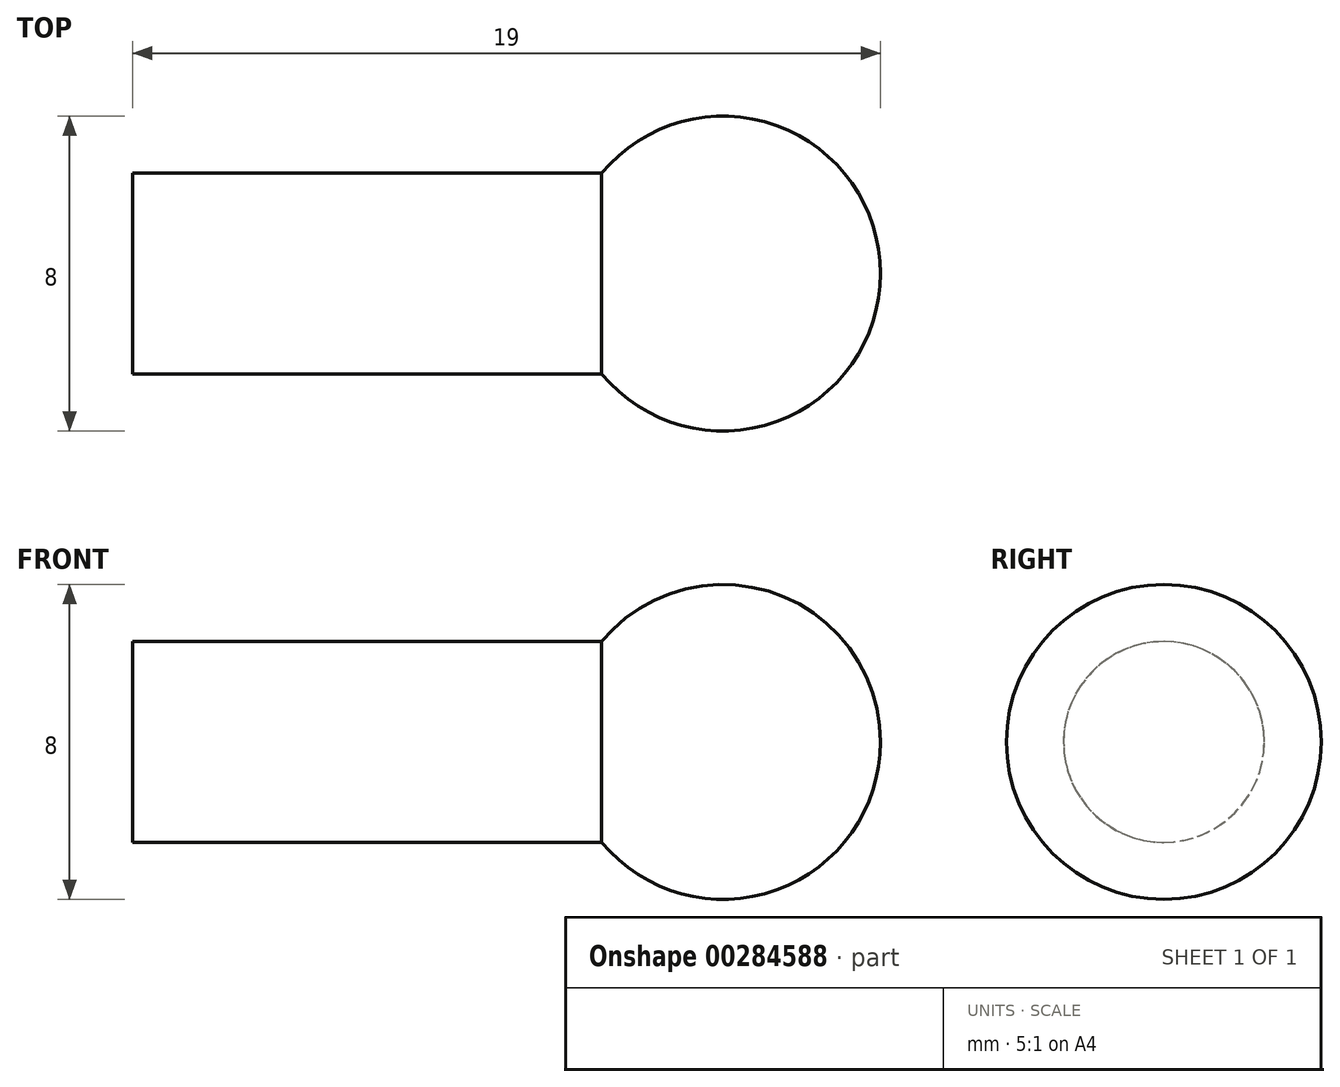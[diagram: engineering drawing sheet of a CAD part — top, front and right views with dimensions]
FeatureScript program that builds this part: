
annotation { "Feature Type Name" : "Feature", "Feature Type Description" : "" }
export const myFeature = defineFeature(function(context is Context, id is Id, definition is map)
    precondition{}
    {
        {
            var Q0;
            Q0=qCreatedBy(makeId("Front.planeOp"),FACE);
            var sketch = newSketch(context, id + "F0", { "sketchPlane" : qUnion([Q0])});
            skLineSegment(sketch, "E0", {"start": v(0, 2.55) * mm, "end": v(-12, 2.55) * mm});
            skLineSegment(sketch, "E1", {"start": v(-12, 2.55) * mm, "end": v(-12, 0) * mm});
            skLineSegment(sketch, "E2", {"start": v(-12, 0) * mm, "end": v(0, 0) * mm});
            skLineSegment(sketch, "E3", {"start": v(0, 2.55) * mm, "end": v(0, 0) * mm});
            skPoint(sketch, "E4.start.orphan", {"position": v(0, 5) * mm});
            skArc(sketch, "E5", {"start": v(-1, 0) * mm, "mid": v(3, -4) * mm, "end": v(7, 0) * mm});
            skLineSegment(sketch, "E6", {"start": v(-1, 0) * mm, "end": v(7, 0) * mm});
            skSolve(sketch);
        }
        {
            var Q0;
            Q0=makeQuery(id+"F0.imprint","IMPRINT",FACE,{"disambiguationData":[TD([[makeQuery(id+"F0.imprint","IMPRINT",EDGE,{"derivedFrom":sQuery(id+"F0.wireOp",EDGE,"E0")}),1.0]])]});
            var Q1;
            Q1=sQuery(id+"F0.wireOp",EDGE,"E2");
            revolve(context, id + "F1", {"entities" : qUnion([Q0]), "axis" : qUnion([Q1]), "revolveType" : RevolveType.FULL});
        }
        {
            var Q0;
            {var subQ0=sQuery(id+"F0.wireOp",EDGE,"E5");Q0=makeQuery(id+"F0.imprint","IMPRINT",FACE,{"disambiguationData":[TD([[makeQuery(id+"F0.imprint","IMPRINT",EDGE,{"derivedFrom":subQ0}),1.0]])]});}
            var Q1;
            Q1=sQuery(id+"F0.wireOp",EDGE,"E6");
            revolve(context, id + "F2", {"operationType" : NewBodyOperationType.ADD, "entities" : qUnion([Q0]), "axis" : qUnion([Q1]), "revolveType" : RevolveType.FULL});
        }
    });
